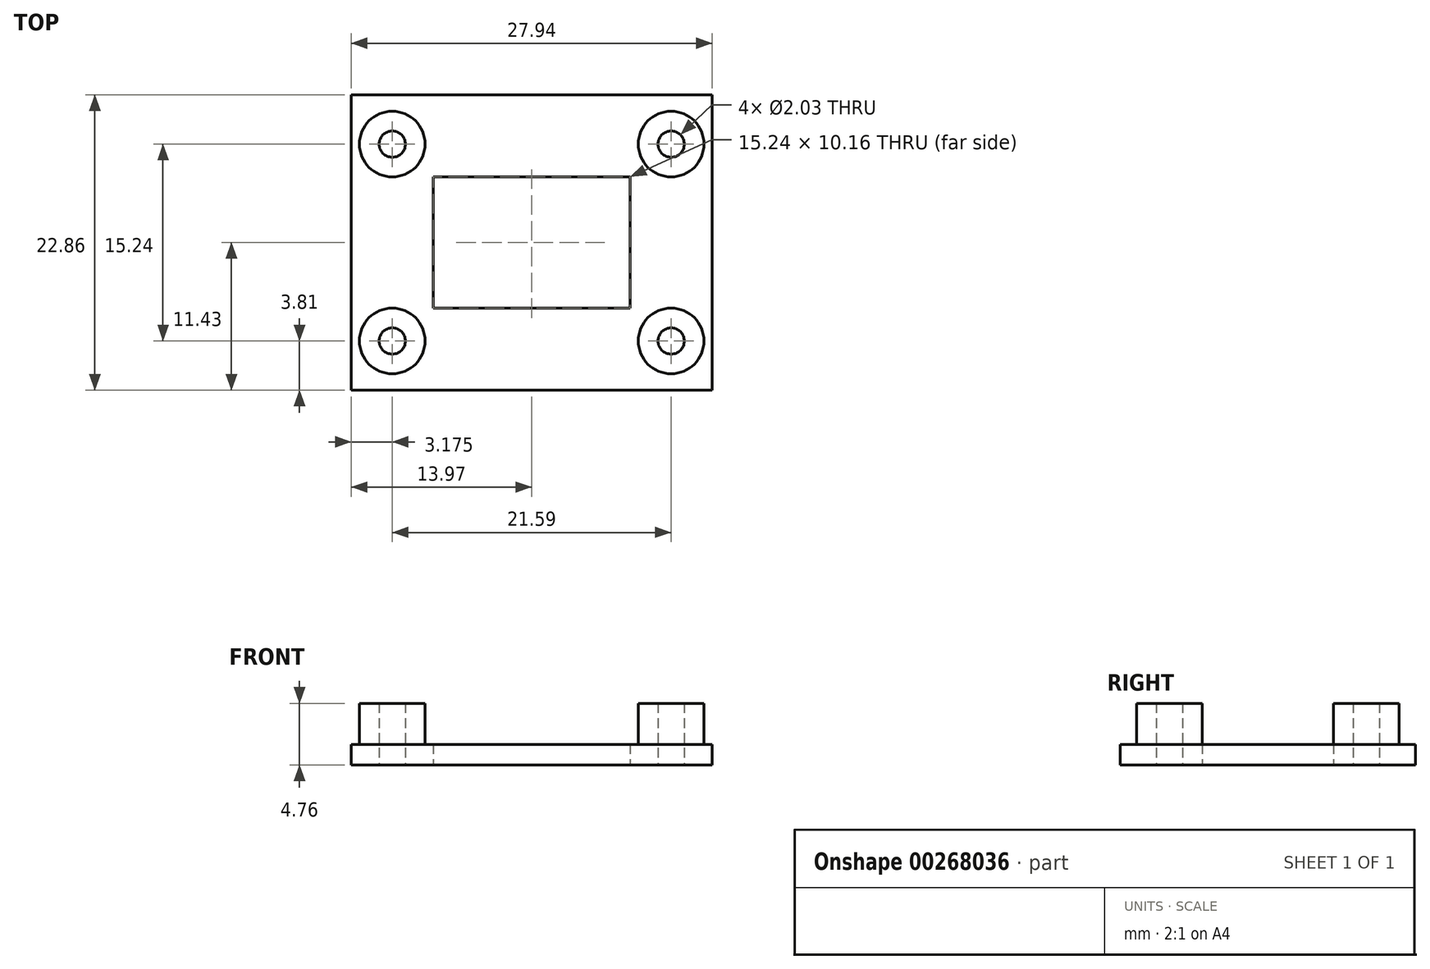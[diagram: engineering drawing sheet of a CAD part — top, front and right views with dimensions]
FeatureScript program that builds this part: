
annotation { "Feature Type Name" : "Feature", "Feature Type Description" : "" }
export const myFeature = defineFeature(function(context is Context, id is Id, definition is map)
    precondition{}
    {
        {
            var Q0;
            Q0=qCreatedBy(makeId("Top.planeOp"),FACE);
            var sketch = newSketch(context, id + "F0", { "sketchPlane" : qUnion([Q0])});
            skLineSegment(sketch, "E0.bottom", {"start": v(13.97, 11.43) * mm, "end": v(-13.97, 11.43) * mm});
            skLineSegment(sketch, "E0.top", {"start": v(13.97, -11.43) * mm, "end": v(-13.97, -11.43) * mm});
            skLineSegment(sketch, "E0.left", {"start": v(13.97, 11.43) * mm, "end": v(13.97, -11.43) * mm});
            skLineSegment(sketch, "E0.right", {"start": v(-13.97, 11.43) * mm, "end": v(-13.97, -11.43) * mm});
            skPoint(sketch, "E0.middle", {"position": v(0, 0) * mm});
            skLineSegment(sketch, "E1.bottom", {"start": v(7.62, 5.08) * mm, "end": v(-7.62, 5.08) * mm});
            skLineSegment(sketch, "E1.top", {"start": v(7.62, -5.08) * mm, "end": v(-7.62, -5.08) * mm});
            skLineSegment(sketch, "E1.left", {"start": v(7.62, 5.08) * mm, "end": v(7.62, -5.08) * mm});
            skLineSegment(sketch, "E1.right", {"start": v(-7.62, 5.08) * mm, "end": v(-7.62, -5.08) * mm});
            skSolve(sketch);
        }
        {
            var Q0;
            Q0=makeQuery(id+"F0.imprint","IMPRINT",FACE,{"disambiguationData":[TD([[makeQuery(id+"F0.imprint","IMPRINT",EDGE,{"derivedFrom":sQuery(id+"F0.wireOp",EDGE,"E0.bottom")}),1.0]])]});
            extrude(context, id + "F1", {"entities" : qUnion([Q0]), "depth" : 1.59 * mm, "offsetDistance" : 25.4 * mm});
        }
        {
            var Q0;
            Q0=makeQuery(id+"F1.opExtrude","CAP_FACE",FACE,{"disambiguationData":[OSD([sQuery(id+"F0.wireOp",EDGE,"E0.bottom"),sQuery(id+"F0.wireOp",EDGE,"E0.top"),sQuery(id+"F0.wireOp",EDGE,"E0.left"),sQuery(id+"F0.wireOp",EDGE,"E0.right"),sQuery(id+"F0.wireOp",EDGE,"E1.bottom"),sQuery(id+"F0.wireOp",EDGE,"E1.top"),sQuery(id+"F0.wireOp",EDGE,"E1.left"),sQuery(id+"F0.wireOp",EDGE,"E1.right")])],"isStart":false});
            var sketch = newSketch(context, id + "F2", { "sketchPlane" : qUnion([Q0])});
            skLineSegment(sketch, "E2.bottom", {"start": v(10.8, -7.62) * mm, "end": v(-10.8, -7.62) * mm, "construction": true});
            skLineSegment(sketch, "E2.top", {"start": v(10.8, 7.62) * mm, "end": v(-10.8, 7.62) * mm, "construction": true});
            skLineSegment(sketch, "E2.left", {"start": v(10.8, -7.62) * mm, "end": v(10.8, 7.62) * mm, "construction": true});
            skLineSegment(sketch, "E2.right", {"start": v(-10.8, -7.62) * mm, "end": v(-10.8, 7.62) * mm, "construction": true});
            skPoint(sketch, "E2.middle", {"position": v(0, 0) * mm});
            skCircle(sketch, "E3", {"center": v(10.8, 7.62) * mm, "radius": 2.54 * mm});
            skCircle(sketch, "E4", {"center": v(10.8, 7.62) * mm, "radius": 1.02 * mm});
            skCircle(sketch, "E5", {"center": v(10.8, -7.62) * mm, "radius": 1.02 * mm});
            skCircle(sketch, "E6", {"center": v(10.8, -7.62) * mm, "radius": 2.54 * mm});
            skCircle(sketch, "E7", {"center": v(-10.8, -7.62) * mm, "radius": 1.02 * mm});
            skCircle(sketch, "E8", {"center": v(-10.8, -7.62) * mm, "radius": 2.54 * mm});
            skCircle(sketch, "E9", {"center": v(-10.8, 7.62) * mm, "radius": 1.02 * mm});
            skCircle(sketch, "E10", {"center": v(-10.8, 7.62) * mm, "radius": 2.54 * mm});
            skSolve(sketch);
        }
        {
            var Q0;
            Q0=makeQuery(id+"F2.imprint","IMPRINT",FACE,{"disambiguationData":[TD([[makeQuery(id+"F2.imprint","IMPRINT",EDGE,{"derivedFrom":sQuery(id+"F2.wireOp",EDGE,"E7")}),-1.0]])]});
            var Q1;
            Q1=makeQuery(id+"F2.imprint","IMPRINT",FACE,{"disambiguationData":[TD([[makeQuery(id+"F2.imprint","IMPRINT",EDGE,{"derivedFrom":sQuery(id+"F2.wireOp",EDGE,"E9")}),-1.0]])]});
            var Q2;
            Q2=makeQuery(id+"F2.imprint","IMPRINT",FACE,{"disambiguationData":[TD([[makeQuery(id+"F2.imprint","IMPRINT",EDGE,{"derivedFrom":sQuery(id+"F2.wireOp",EDGE,"E5")}),-1.0]])]});
            var Q3;
            Q3=makeQuery(id+"F2.imprint","IMPRINT",FACE,{"disambiguationData":[TD([[makeQuery(id+"F2.imprint","IMPRINT",EDGE,{"derivedFrom":sQuery(id+"F2.wireOp",EDGE,"E3")}),1.0]])]});
            extrude(context, id + "F3", {"entities" : qUnion([Q0, Q1, Q2, Q3]), "operationType" : NewBodyOperationType.ADD, "depth" : 3.17 * mm, "offsetDistance" : 25.4 * mm});
        }
        {
            var Q0;
            Q0=makeQuery(id+"F2.imprint","IMPRINT",FACE,{"disambiguationData":[TD([[makeQuery(id+"F2.imprint","IMPRINT",EDGE,{"derivedFrom":sQuery(id+"F2.wireOp",EDGE,"E5")}),1.0]])]});
            var Q1;
            Q1=makeQuery(id+"F2.imprint","IMPRINT",FACE,{"disambiguationData":[TD([[makeQuery(id+"F2.imprint","IMPRINT",EDGE,{"derivedFrom":sQuery(id+"F2.wireOp",EDGE,"E4")}),1.0]])]});
            var Q2;
            Q2=makeQuery(id+"F2.imprint","IMPRINT",FACE,{"disambiguationData":[TD([[makeQuery(id+"F2.imprint","IMPRINT",EDGE,{"derivedFrom":sQuery(id+"F2.wireOp",EDGE,"E9")}),1.0]])]});
            var Q3;
            Q3=makeQuery(id+"F2.imprint","IMPRINT",FACE,{"disambiguationData":[TD([[makeQuery(id+"F2.imprint","IMPRINT",EDGE,{"derivedFrom":sQuery(id+"F2.wireOp",EDGE,"E7")}),1.0]])]});
            extrude(context, id + "F4", {"entities" : qUnion([Q0, Q1, Q2, Q3]), "operationType" : NewBodyOperationType.REMOVE, "oppositeDirection" : true, "depth" : 25.4 * mm, "offsetDistance" : 25.4 * mm});
        }
    });
